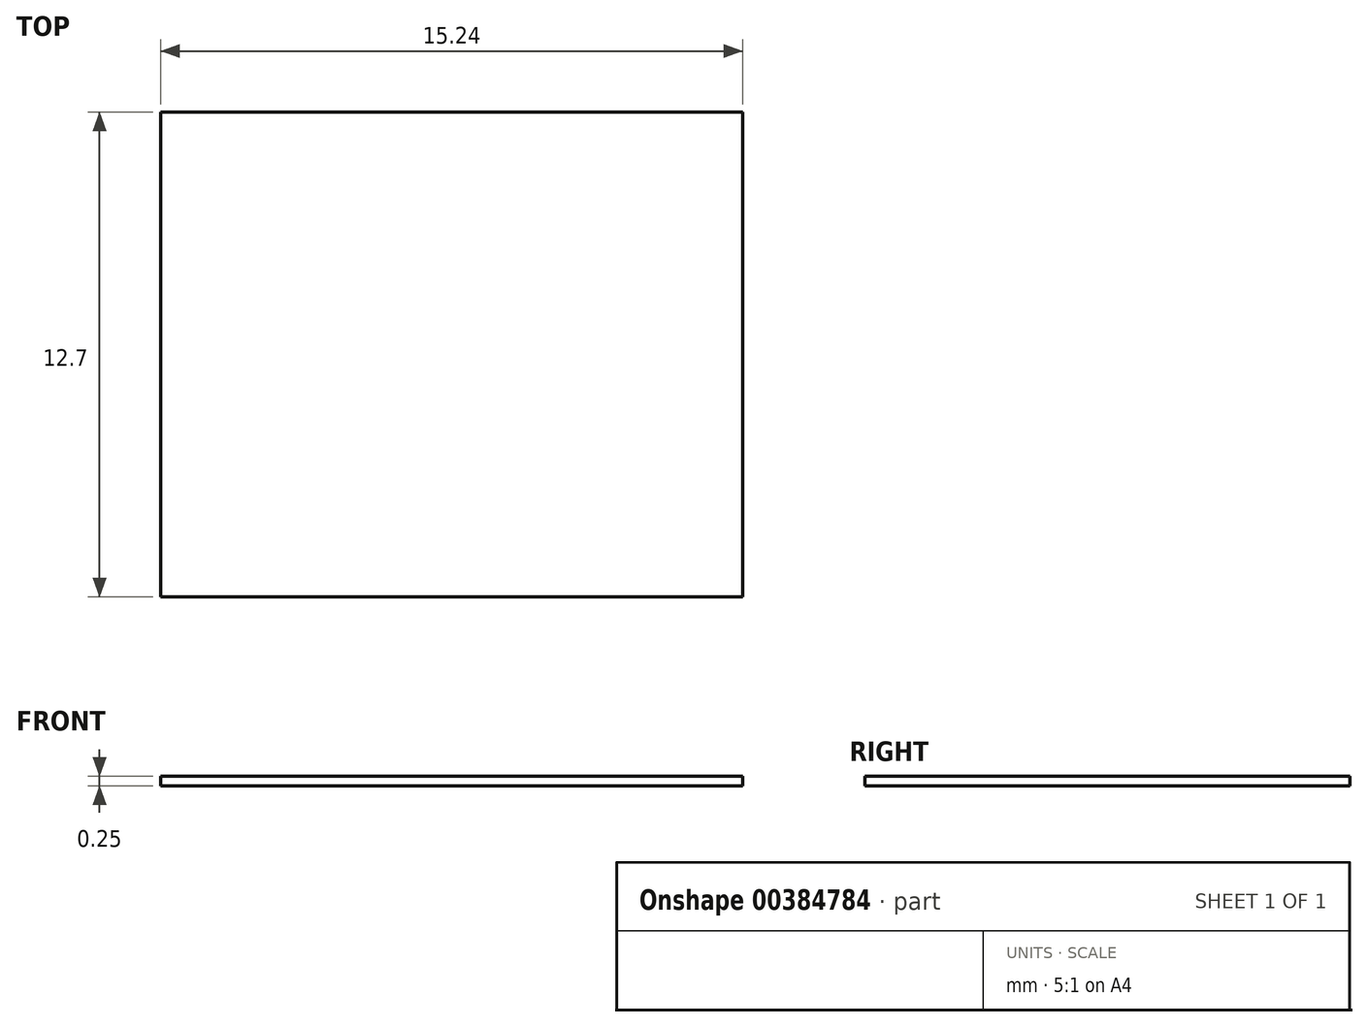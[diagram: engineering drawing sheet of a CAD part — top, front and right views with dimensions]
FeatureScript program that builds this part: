
annotation { "Feature Type Name" : "Feature", "Feature Type Description" : "" }
export const myFeature = defineFeature(function(context is Context, id is Id, definition is map)
    precondition{}
    {
        {
            var Q0;
            Q0=qCreatedBy(makeId("Top.planeOp"),FACE);
            var sketch = newSketch(context, id + "F0", { "sketchPlane" : qUnion([Q0])});
            skLineSegment(sketch, "E0.bottom", {"start": v(-52.54, 53.2) * mm, "end": v(-37.3, 53.2) * mm});
            skLineSegment(sketch, "E0.top", {"start": v(-52.54, 40.5) * mm, "end": v(-37.3, 40.5) * mm});
            skLineSegment(sketch, "E0.left", {"start": v(-52.54, 53.2) * mm, "end": v(-52.54, 40.5) * mm});
            skLineSegment(sketch, "E0.right", {"start": v(-37.3, 53.2) * mm, "end": v(-37.3, 40.5) * mm});
            skSolve(sketch);
        }
        {
            var Q0;
            Q0=makeQuery(id+"F0.imprint","IMPRINT",FACE,{"disambiguationData":[TD([[makeQuery(id+"F0.imprint","IMPRINT",EDGE,{"derivedFrom":sQuery(id+"F0.wireOp",EDGE,"E0.bottom")}),-1.0]])]});
            extrude(context, id + "F1", {"entities" : qUnion([Q0]), "depth" : 0.25 * mm});
        }
    });
